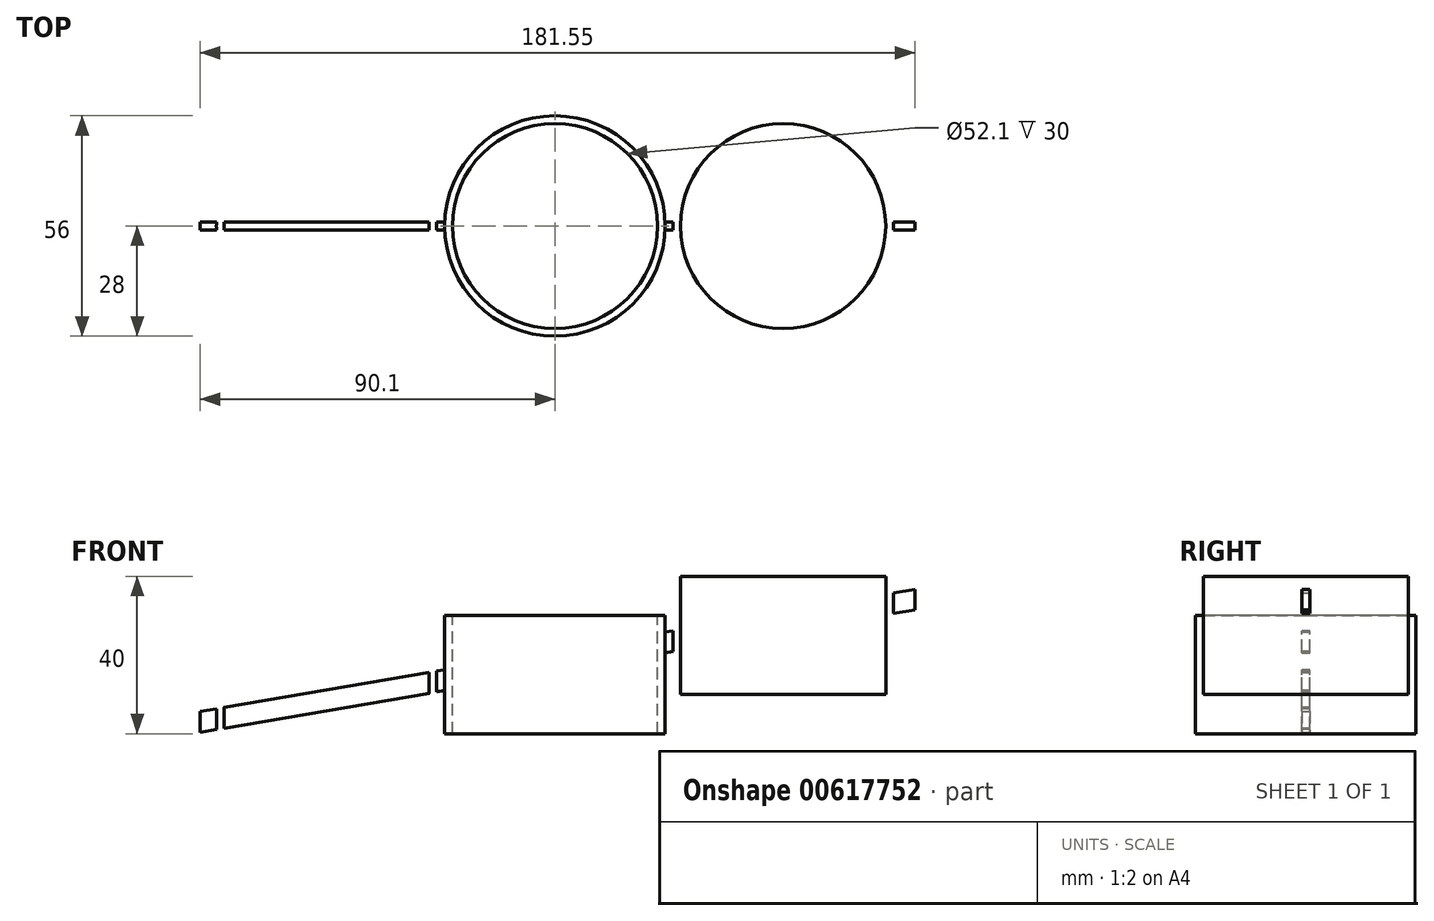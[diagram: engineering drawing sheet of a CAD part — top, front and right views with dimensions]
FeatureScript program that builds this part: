
annotation { "Feature Type Name" : "Feature", "Feature Type Description" : "" }
export const myFeature = defineFeature(function(context is Context, id is Id, definition is map)
    precondition{}
    {
        {
            var Q0;
            Q0=qCreatedBy(makeId("Top.planeOp"),FACE);
            var sketch = newSketch(context, id + "F0", { "sketchPlane" : qUnion([Q0])});
            skCircle(sketch, "E0", {"center": v(0, 0) * mm, "radius": 26.05 * mm});
            skCircle(sketch, "E1", {"center": v(0, 0) * mm, "radius": 28 * mm});
            skCircle(sketch, "E2", {"center": v(0, 0) * mm, "radius": 29 * mm, "construction": true});
            skLineSegment(sketch, "E3", {"start": v(-29, 0) * mm, "end": v(-29, 46.74) * mm, "construction": true});
            skLineSegment(sketch, "E4", {"start": v(29, 0) * mm, "end": v(29, 46.34) * mm, "construction": true});
            skCircle(sketch, "E5.MirrorC", {"center": v(-58, 0) * mm, "radius": 28 * mm});
            skCircle(sketch, "E6.MirrorC", {"center": v(-58, 0) * mm, "radius": 26.05 * mm});
            skCircle(sketch, "E7.MirrorC", {"center": v(58, 0) * mm, "radius": 26.05 * mm});
            skCircle(sketch, "E8.MirrorC", {"center": v(58, 0) * mm, "radius": 28 * mm});
            skSolve(sketch);
        }
        {
            var Q0;
            Q0=makeQuery(id+"F0.imprint","IMPRINT",FACE,{"disambiguationData":[TD([[makeQuery(id+"F0.imprint","IMPRINT",EDGE,{"derivedFrom":sQuery(id+"F0.wireOp",EDGE,"E7.MirrorC")}),1.0]])]});
            var Q1;
            Q1=makeQuery(id+"F0.imprint","IMPRINT",FACE,{"disambiguationData":[TD([[makeQuery(id+"F0.imprint","IMPRINT",EDGE,{"derivedFrom":sQuery(id+"F0.wireOp",EDGE,"E7.MirrorC")}),-1.0]])]});
            var Q2;
            Q2=sQuery(id+"F0.wireOp",EDGE,"E5.MirrorC");
            var Q3;
            Q3=sQuery(id+"F0.wireOp",EDGE,"E1");
            var Q4;
            Q4=sQuery(id+"F0.wireOp",EDGE,"E8.MirrorC");
            var Q5;
            Q5=sQuery(id+"F0.wireOp",EDGE,"E7.MirrorC");
            extrude(context, id + "F1", {"entities" : qUnion([Q0, Q1]), "surfaceEntities" : qUnion([Q2, Q3, Q4, Q5]), "oppositeDirection" : true, "depth" : 30 * mm, "offsetDistance" : 25 * mm});
        }
        {
            var Q0;
            Q0=makeQuery(id+"F0.imprint","IMPRINT",FACE,{"disambiguationData":[TD([[makeQuery(id+"F0.imprint","IMPRINT",EDGE,{"derivedFrom":sQuery(id+"F0.wireOp",EDGE,"E0")}),-1.0]])]});
            var Q1;
            Q1=makeQuery(id+"F0.imprint","IMPRINT",FACE,{"disambiguationData":[TD([[makeQuery(id+"F0.imprint","IMPRINT",EDGE,{"derivedFrom":sQuery(id+"F0.wireOp",EDGE,"E0")}),1.0]])]});
            var Q2;
            Q2=sQuery(id+"F0.wireOp",EDGE,"E0");
            var Q3;
            Q3=sQuery(id+"F0.wireOp",EDGE,"E1");
            extrude(context, id + "F2", {"entities" : qUnion([Q0, Q1]), "surfaceEntities" : qUnion([Q2, Q3]), "oppositeDirection" : true, "depth" : 40 * mm, "offsetDistance" : 25 * mm, "hasSecondDirection" : true, "secondDirectionOppositeDirection" : true, "secondDirectionDepth" : 10 * mm});
        }
        {
            var Q0;
            Q0=makeQuery(id+"F0.imprint","IMPRINT",FACE,{"disambiguationData":[TD([[makeQuery(id+"F0.imprint","IMPRINT",EDGE,{"derivedFrom":sQuery(id+"F0.wireOp",EDGE,"E5.MirrorC")}),-1.0]])]});
            var Q1;
            Q1=makeQuery(id+"F0.imprint","IMPRINT",FACE,{"disambiguationData":[TD([[makeQuery(id+"F0.imprint","IMPRINT",EDGE,{"derivedFrom":sQuery(id+"F0.wireOp",EDGE,"E6.MirrorC")}),-1.0]])]});
            var Q2;
            Q2=sQuery(id+"F0.wireOp",EDGE,"E5.MirrorC");
            var Q3;
            Q3=sQuery(id+"F0.wireOp",EDGE,"E6.MirrorC");
            extrude(context, id + "F3", {"entities" : qUnion([Q0, Q1]), "surfaceEntities" : qUnion([Q2, Q3]), "oppositeDirection" : true, "depth" : 50 * mm, "offsetDistance" : 25 * mm, "hasSecondDirection" : true, "secondDirectionOppositeDirection" : true, "secondDirectionDepth" : 20 * mm});
        }
        {
            var Q0;
            Q0=qCreatedBy(makeId("Front.planeOp"),FACE);
            var sketch = newSketch(context, id + "F4", { "sketchPlane" : qUnion([Q0])});
            skLineSegment(sketch, "E9", {"start": v(-90.1, -34.4) * mm, "end": v(91.45, -3.3) * mm});
            skLineSegment(sketch, "E10", {"start": v(-90.1, -39.65) * mm, "end": v(91.45, -8.56) * mm});
            skLineSegment(sketch, "E11", {"start": v(91.45, -3.3) * mm, "end": v(91.45, -8.56) * mm});
            skLineSegment(sketch, "E12", {"start": v(-90.1, -34.4) * mm, "end": v(-90.1, -39.65) * mm});
            skSolve(sketch);
        }
        {
            var Q0;
            Q0 = qSketchRegion(id + "F4", true);
            extrude(context, id + "F5", {"entities" : qUnion([Q0]), "operationType" : NewBodyOperationType.ADD, "depth" : 1 * mm, "offsetDistance" : 25 * mm, "hasSecondDirection" : true, "secondDirectionOppositeDirection" : true, "secondDirectionDepth" : 1 * mm});
        }
        {
            var Q0;
            Q0=makeQuery(id+"F0.imprint","IMPRINT",FACE,{"disambiguationData":[TD([[makeQuery(id+"F0.imprint","IMPRINT",EDGE,{"derivedFrom":sQuery(id+"F0.wireOp",EDGE,"E6.MirrorC")}),-1.0]])]});
            extrude(context, id + "F6", {"entities" : qUnion([Q0]), "operationType" : NewBodyOperationType.REMOVE, "oppositeDirection" : true, "depth" : 50 * mm, "offsetDistance" : 25 * mm});
        }
        {
            var Q0;
            Q0=makeQuery(id+"F0.imprint","IMPRINT",FACE,{"disambiguationData":[TD([[makeQuery(id+"F0.imprint","IMPRINT",EDGE,{"derivedFrom":sQuery(id+"F0.wireOp",EDGE,"E0")}),1.0]])]});
            extrude(context, id + "F7", {"entities" : qUnion([Q0]), "operationType" : NewBodyOperationType.REMOVE, "oppositeDirection" : true, "depth" : 150.7 * mm, "offsetDistance" : 25 * mm});
        }
        {
            var Q0;
            Q0=makeQuery(id+"F0.imprint","IMPRINT",FACE,{"disambiguationData":[TD([[makeQuery(id+"F0.imprint","IMPRINT",EDGE,{"derivedFrom":sQuery(id+"F0.wireOp",EDGE,"E7.MirrorC")}),-1.0]])]});
            extrude(context, id + "F8", {"entities" : qUnion([Q0]), "operationType" : NewBodyOperationType.REMOVE, "oppositeDirection" : true, "depth" : 50 * mm, "offsetDistance" : 25 * mm});
        }
    });
